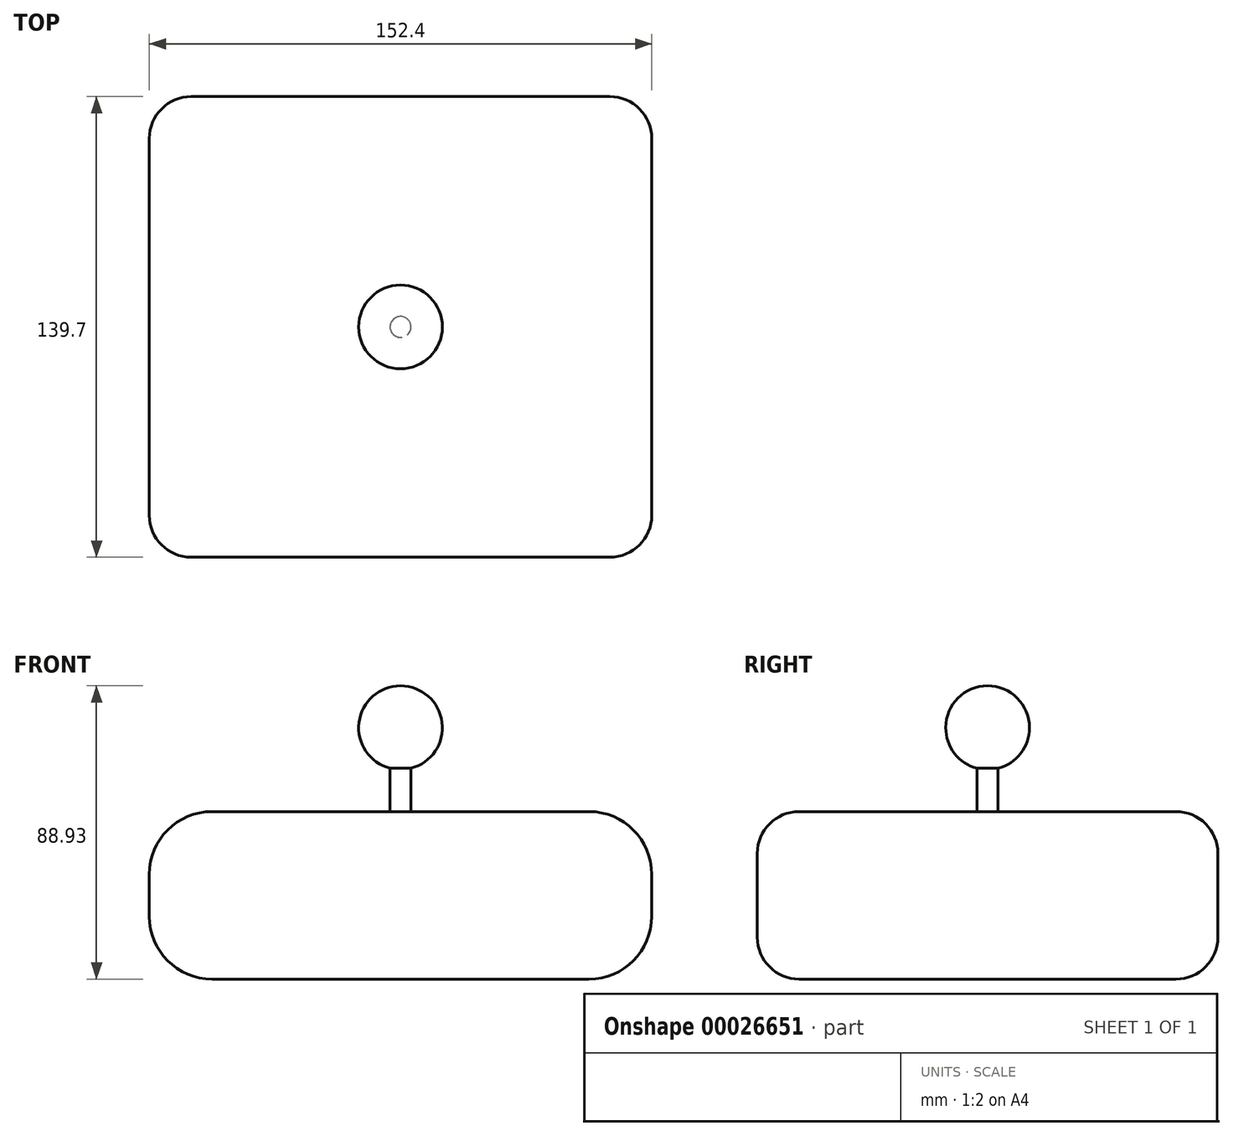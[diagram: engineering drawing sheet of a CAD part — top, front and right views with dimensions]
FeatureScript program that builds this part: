
annotation { "Feature Type Name" : "Feature", "Feature Type Description" : "" }
export const myFeature = defineFeature(function(context is Context, id is Id, definition is map)
    precondition{}
    {
        {
            var Q0;
            Q0=qCreatedBy(makeId("Front.planeOp"),FACE);
            var sketch = newSketch(context, id + "F0", { "sketchPlane" : qUnion([Q0])});
            skLineSegment(sketch, "E0.rect.bottom", {"start": v(-57.15, 25.4) * mm, "end": v(57.15, 25.4) * mm});
            skLineSegment(sketch, "E0.rect.top", {"start": v(-57.15, -25.4) * mm, "end": v(57.15, -25.4) * mm});
            skLineSegment(sketch, "E0.rect.left", {"start": v(-76.2, 6.35) * mm, "end": v(-76.2, -6.35) * mm});
            skLineSegment(sketch, "E0.rect.right", {"start": v(76.2, 6.35) * mm, "end": v(76.2, -6.35) * mm});
            skPoint(sketch, "E0.rect.middle", {"position": v(0, 0) * mm});
            skPoint(sketch, "E1.visualSharp", {"position": v(76.2, 25.4) * mm});
            skArc(sketch, "E1.filletArc", {"start": v(76.2, 6.35) * mm, "mid": v(70.62, 19.82) * mm, "end": v(57.15, 25.4) * mm});
            skPoint(sketch, "E2.visualSharp", {"position": v(76.2, -25.4) * mm});
            skArc(sketch, "E2.filletArc", {"start": v(57.15, -25.4) * mm, "mid": v(70.62, -19.82) * mm, "end": v(76.2, -6.35) * mm});
            skPoint(sketch, "E3.visualSharp", {"position": v(-76.2, -25.4) * mm});
            skArc(sketch, "E3.filletArc", {"start": v(-76.2, -6.35) * mm, "mid": v(-70.62, -19.82) * mm, "end": v(-57.15, -25.4) * mm});
            skPoint(sketch, "E4.visualSharp", {"position": v(-76.2, 25.4) * mm});
            skArc(sketch, "E4.filletArc", {"start": v(-57.15, 25.4) * mm, "mid": v(-70.62, 19.82) * mm, "end": v(-76.2, 6.35) * mm});
            skSolve(sketch);
        }
        {
            var Q0;
            Q0=makeQuery(id+"F0.imprint","IMPRINT",FACE,{"disambiguationData":[TD([[makeQuery(id+"F0.imprint","IMPRINT",EDGE,{"derivedFrom":sQuery(id+"F0.wireOp",EDGE,"E0.rect.bottom")}),-1.0]])]});
            extrude(context, id + "F1", {"entities" : qUnion([Q0]), "depth" : 139.7 * mm});
        }
        {
            var Q0;
            Q0=makeQuery(id+"F1.opExtrude","CAP_EDGE",EDGE,{"disambiguationData":[OSD([sQuery(id+"F0.wireOp",EDGE,"E0.rect.bottom")])],"isStart":false});
            var Q1;
            Q1=makeQuery(id+"F1.opExtrude","CAP_EDGE",EDGE,{"disambiguationData":[OSD([sQuery(id+"F0.wireOp",EDGE,"E4.filletArc")])],"isStart":false});
            var Q2;
            Q2=makeQuery(id+"F1.opExtrude","CAP_EDGE",EDGE,{"disambiguationData":[OSD([sQuery(id+"F0.wireOp",EDGE,"E0.rect.left")])],"isStart":false});
            var Q3;
            Q3=makeQuery(id+"F1.opExtrude","CAP_EDGE",EDGE,{"disambiguationData":[OSD([sQuery(id+"F0.wireOp",EDGE,"E3.filletArc")])],"isStart":false});
            var Q4;
            Q4=makeQuery(id+"F1.opExtrude","CAP_EDGE",EDGE,{"disambiguationData":[OSD([sQuery(id+"F0.wireOp",EDGE,"E0.rect.top")])],"isStart":false});
            var Q5;
            Q5=makeQuery(id+"F1.opExtrude","CAP_EDGE",EDGE,{"disambiguationData":[OSD([sQuery(id+"F0.wireOp",EDGE,"E1.filletArc")])],"isStart":false});
            var Q6;
            Q6=makeQuery(id+"F1.opExtrude","CAP_EDGE",EDGE,{"disambiguationData":[OSD([sQuery(id+"F0.wireOp",EDGE,"E0.rect.right")])],"isStart":false});
            var Q7;
            Q7=makeQuery(id+"F1.opExtrude","CAP_EDGE",EDGE,{"disambiguationData":[OSD([sQuery(id+"F0.wireOp",EDGE,"E2.filletArc")])],"isStart":false});
            var Q8;
            Q8=makeQuery(id+"F1.opExtrude","CAP_EDGE",EDGE,{"disambiguationData":[OSD([sQuery(id+"F0.wireOp",EDGE,"E0.rect.bottom")])],"isStart":true});
            var Q9;
            Q9=makeQuery(id+"F1.opExtrude","CAP_EDGE",EDGE,{"disambiguationData":[OSD([sQuery(id+"F0.wireOp",EDGE,"E1.filletArc")])],"isStart":true});
            var Q10;
            Q10=makeQuery(id+"F1.opExtrude","CAP_EDGE",EDGE,{"disambiguationData":[OSD([sQuery(id+"F0.wireOp",EDGE,"E0.rect.right")])],"isStart":true});
            var Q11;
            Q11=makeQuery(id+"F1.opExtrude","CAP_EDGE",EDGE,{"disambiguationData":[OSD([sQuery(id+"F0.wireOp",EDGE,"E2.filletArc")])],"isStart":true});
            var Q12;
            Q12=makeQuery(id+"F1.opExtrude","CAP_EDGE",EDGE,{"disambiguationData":[OSD([sQuery(id+"F0.wireOp",EDGE,"E0.rect.top")])],"isStart":true});
            var Q13;
            Q13=makeQuery(id+"F1.opExtrude","CAP_EDGE",EDGE,{"disambiguationData":[OSD([sQuery(id+"F0.wireOp",EDGE,"E0.rect.left")])],"isStart":true});
            var Q14;
            Q14=makeQuery(id+"F1.opExtrude","CAP_EDGE",EDGE,{"disambiguationData":[OSD([sQuery(id+"F0.wireOp",EDGE,"E4.filletArc")])],"isStart":true});
            var Q15;
            Q15=makeQuery(id+"F1.opExtrude","CAP_EDGE",EDGE,{"disambiguationData":[OSD([sQuery(id+"F0.wireOp",EDGE,"E3.filletArc")])],"isStart":true});
            fillet(context, id + "F2", {"entities" : qUnion([Q0, Q1, Q2, Q3, Q4, Q5, Q6, Q7, Q8, Q9, Q10, Q11, Q12, Q13, Q14, Q15]), "radius" : 12.7 * mm, "tangentPropagation" : true, "allowEdgeOverflow" : false});
        }
        {
            var Q0;
            Q0=makeQuery(id+"F1.opExtrude","SWEPT_FACE",FACE,{"disambiguationData":[OSD([sQuery(id+"F0.wireOp",EDGE,"E0.rect.bottom")])]});
            var sketch = newSketch(context, id + "F3", { "sketchPlane" : qUnion([Q0])});
            skPoint(sketch, "E5.orphan", {"position": v(0, -12.7) * mm});
            skPoint(sketch, "E6.orphan", {"position": v(57.15, -69.85) * mm});
            skPoint(sketch, "E7.start.orphan", {"position": v(0, -127) * mm});
            skPoint(sketch, "E8.start.orphan", {"position": v(-57.15, -69.85) * mm});
            skPoint(sketch, "E9", {"position": v(0, -69.85) * mm});
            skCircle(sketch, "E10", {"center": v(0, -69.85) * mm, "radius": 3.18 * mm});
            skSolve(sketch);
        }
        {
            var Q0;
            Q0 = qSketchRegion(id + "F3", true);
            extrude(context, id + "F4", {"entities" : qUnion([Q0]), "operationType" : NewBodyOperationType.ADD, "depth" : 25.4 * mm});
        }
        {
            var Q0;
            Q0=qCreatedBy(makeId("Right.planeOp"),FACE);
            var sketch = newSketch(context, id + "F5", { "sketchPlane" : qUnion([Q0])});
            skLineSegment(sketch, "E11", {"start": v(-82.55, 50.83) * mm, "end": v(-57.15, 50.83) * mm});
            skPoint(sketch, "E12", {"position": v(-69.85, 50.83) * mm});
            skArc(sketch, "E13", {"start": v(-57.15, 50.83) * mm, "mid": v(-69.85, 63.53) * mm, "end": v(-82.55, 50.83) * mm});
            skLineSegment(sketch, "E14", {"start": v(-73.03, 50.83) * mm, "end": v(-66.68, 50.83) * mm});
            skSolve(sketch);
        }
        {
            var Q0;
            {var subQ1=sQuery(id+"F5.wireOp",EDGE,"E11");Q0=makeQuery(id+"F5.imprint","IMPRINT",FACE,{"disambiguationData":[TD([[makeQuery(id+"F5.imprint","IMPRINT",EDGE,{"derivedFrom":subQ1}),1.0]])]});}
            var Q1;
            Q1=sQuery(id+"F5.wireOp",EDGE,"E11");
            revolve(context, id + "F6", {"operationType" : NewBodyOperationType.ADD, "entities" : qUnion([Q0]), "axis" : qUnion([Q1]), "revolveType" : RevolveType.FULL});
        }
    });
